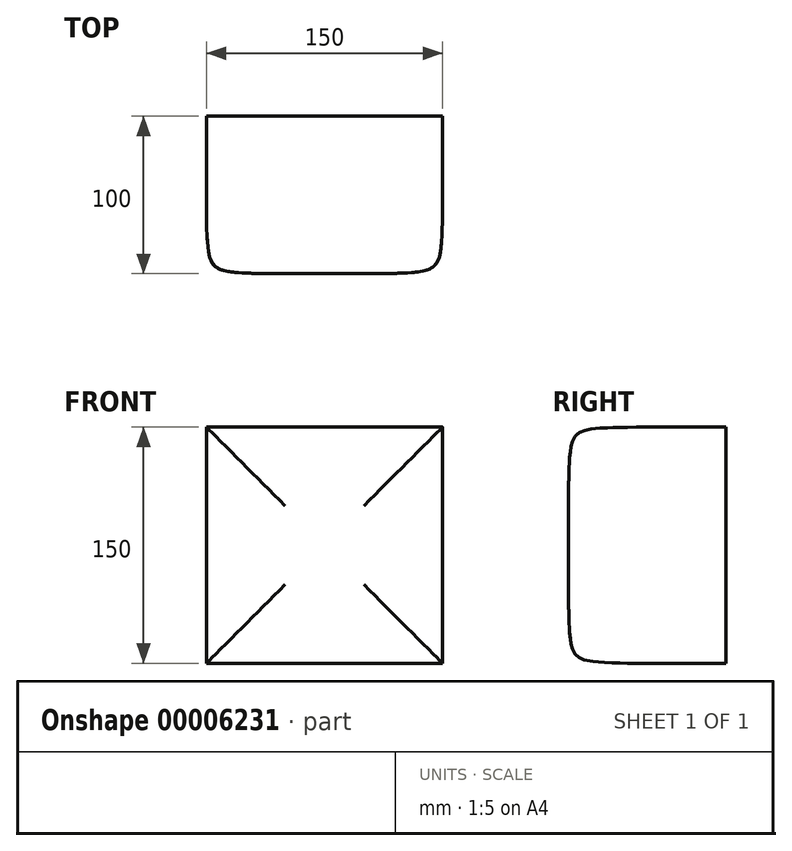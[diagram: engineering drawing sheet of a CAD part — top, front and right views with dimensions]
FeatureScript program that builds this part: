
annotation { "Feature Type Name" : "Feature", "Feature Type Description" : "" }
export const myFeature = defineFeature(function(context is Context, id is Id, definition is map)
    precondition{}
    {
        {
            var Q0;
            Q0=qCreatedBy(makeId("Front.planeOp"),FACE);
            var sketch = newSketch(context, id + "F0", { "sketchPlane" : qUnion([Q0])});
            skLineSegment(sketch, "E0.rect.bottom", {"start": v(75, 75) * mm, "end": v(-75, 75) * mm});
            skLineSegment(sketch, "E0.rect.top", {"start": v(75, -75) * mm, "end": v(-75, -75) * mm});
            skLineSegment(sketch, "E0.rect.left", {"start": v(75, 75) * mm, "end": v(75, -75) * mm});
            skLineSegment(sketch, "E0.rect.right", {"start": v(-75, 75) * mm, "end": v(-75, -75) * mm});
            skPoint(sketch, "E0.rect.middle", {"position": v(0, 0) * mm});
            skSolve(sketch);
        }
        {
            var Q0;
            Q0=makeQuery(id+"F0.imprint","IMPRINT",FACE,{"disambiguationData":[TD([[makeQuery(id+"F0.imprint","IMPRINT",EDGE,{"derivedFrom":sQuery(id+"F0.wireOp",EDGE,"E0.rect.bottom")}),1.0]])]});
            extrude(context, id + "F1", {"entities" : qUnion([Q0]), "depth" : 100 * mm});
        }
        {
            var Q0;
            Q0=makeQuery(id+"F1.opExtrude","CAP_FACE",FACE,{"disambiguationData":[OSD([sQuery(id+"F0.wireOp",EDGE,"E0.rect.bottom"),sQuery(id+"F0.wireOp",EDGE,"E0.rect.top"),sQuery(id+"F0.wireOp",EDGE,"E0.rect.left"),sQuery(id+"F0.wireOp",EDGE,"E0.rect.right")])],"isStart":false});
            fillet(context, id + "F2", {"entities" : qUnion([Q0]), "radius" : 50 * mm, "tangentPropagation" : true, "rho" : 0.8, "crossSection" : FilletCrossSection.CONIC, "allowEdgeOverflow" : false});
        }
    });
